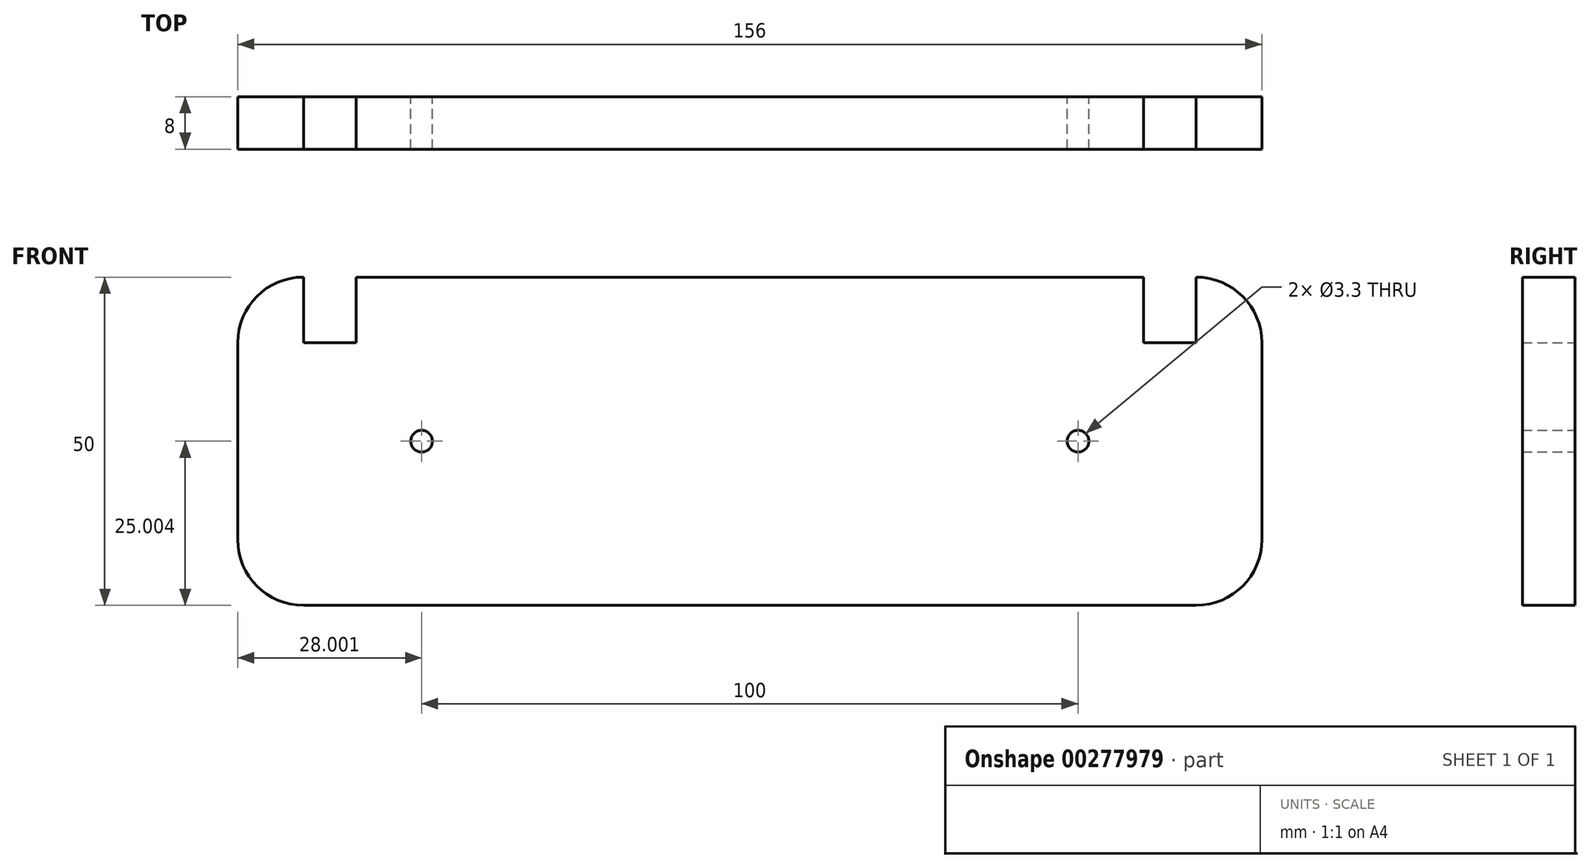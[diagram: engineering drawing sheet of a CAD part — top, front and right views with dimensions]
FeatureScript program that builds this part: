
annotation { "Feature Type Name" : "Feature", "Feature Type Description" : "" }
export const myFeature = defineFeature(function(context is Context, id is Id, definition is map)
    precondition{}
    {
        {
            var Q0;
            Q0=qCreatedBy(makeId("Front.planeOp"),FACE);
            var sketch = newSketch(context, id + "F0", { "sketchPlane" : qUnion([Q0])});
            skLineSegment(sketch, "E0", {"start": v(92.96, 188.6) * mm, "end": v(-27.04, 188.6) * mm});
            skCircle(sketch, "E1", {"center": v(-17.04, 213.6) * mm, "radius": 1.65 * mm});
            skCircle(sketch, "E2", {"center": v(82.96, 213.6) * mm, "radius": 1.65 * mm});
            skLineSegment(sketch, "E3", {"start": v(-27.04, 238.6) * mm, "end": v(92.96, 238.6) * mm});
            skLineSegment(sketch, "E4", {"start": v(-27.04, 238.6) * mm, "end": v(-27.04, 228.6) * mm});
            skLineSegment(sketch, "E5", {"start": v(-27.04, 228.6) * mm, "end": v(-35.04, 228.6) * mm});
            skLineSegment(sketch, "E6", {"start": v(-35.04, 228.6) * mm, "end": v(-35.04, 238.6) * mm});
            skLineSegment(sketch, "E7", {"start": v(-35.04, 238.6) * mm, "end": v(-45.04, 238.6) * mm});
            skLineSegment(sketch, "E8", {"start": v(-45.04, 238.6) * mm, "end": v(-45.04, 188.6) * mm});
            skLineSegment(sketch, "E9", {"start": v(-45.04, 188.6) * mm, "end": v(110.96, 188.6) * mm});
            skLineSegment(sketch, "E10", {"start": v(110.96, 188.6) * mm, "end": v(110.96, 238.6) * mm});
            skLineSegment(sketch, "E11", {"start": v(110.96, 238.6) * mm, "end": v(100.96, 238.6) * mm});
            skLineSegment(sketch, "E12", {"start": v(100.96, 238.6) * mm, "end": v(100.96, 228.6) * mm});
            skLineSegment(sketch, "E13", {"start": v(100.96, 228.6) * mm, "end": v(92.96, 228.6) * mm});
            skLineSegment(sketch, "E14", {"start": v(92.96, 228.6) * mm, "end": v(92.96, 238.6) * mm});
            skSolve(sketch);
        }
        {
            var Q0;
            Q0=qSketchRegion(id+"F0",true);
            extrude(context, id + "F1", {"entities" : qUnion([Q0]), "depth" : 8 * mm});
        }
        {
            var Q0;
            Q0=makeQuery(id+"F1.opExtrude","SWEPT_EDGE",EDGE,{"disambiguationData":[OSD([sQuery(id+"F0.wireOp",EDGE,"E7"),sQuery(id+"F0.wireOp",EDGE,"E8")])]});
            var Q1;
            Q1=makeQuery(id+"F1.opExtrude","SWEPT_EDGE",EDGE,{"disambiguationData":[OSD([sQuery(id+"F0.wireOp",EDGE,"E8"),sQuery(id+"F0.wireOp",EDGE,"E9")])]});
            var Q2;
            Q2=makeQuery(id+"F1.opExtrude","SWEPT_EDGE",EDGE,{"disambiguationData":[OSD([sQuery(id+"F0.wireOp",EDGE,"E9"),sQuery(id+"F0.wireOp",EDGE,"E10")])]});
            var Q3;
            Q3=makeQuery(id+"F1.opExtrude","SWEPT_EDGE",EDGE,{"disambiguationData":[OSD([sQuery(id+"F0.wireOp",EDGE,"E10"),sQuery(id+"F0.wireOp",EDGE,"E11")])]});
            fillet(context, id + "F2", {"entities" : qUnion([Q0, Q1, Q2, Q3]), "radius" : 10 * mm, "tangentPropagation" : true, "allowEdgeOverflow" : false});
        }
    });
